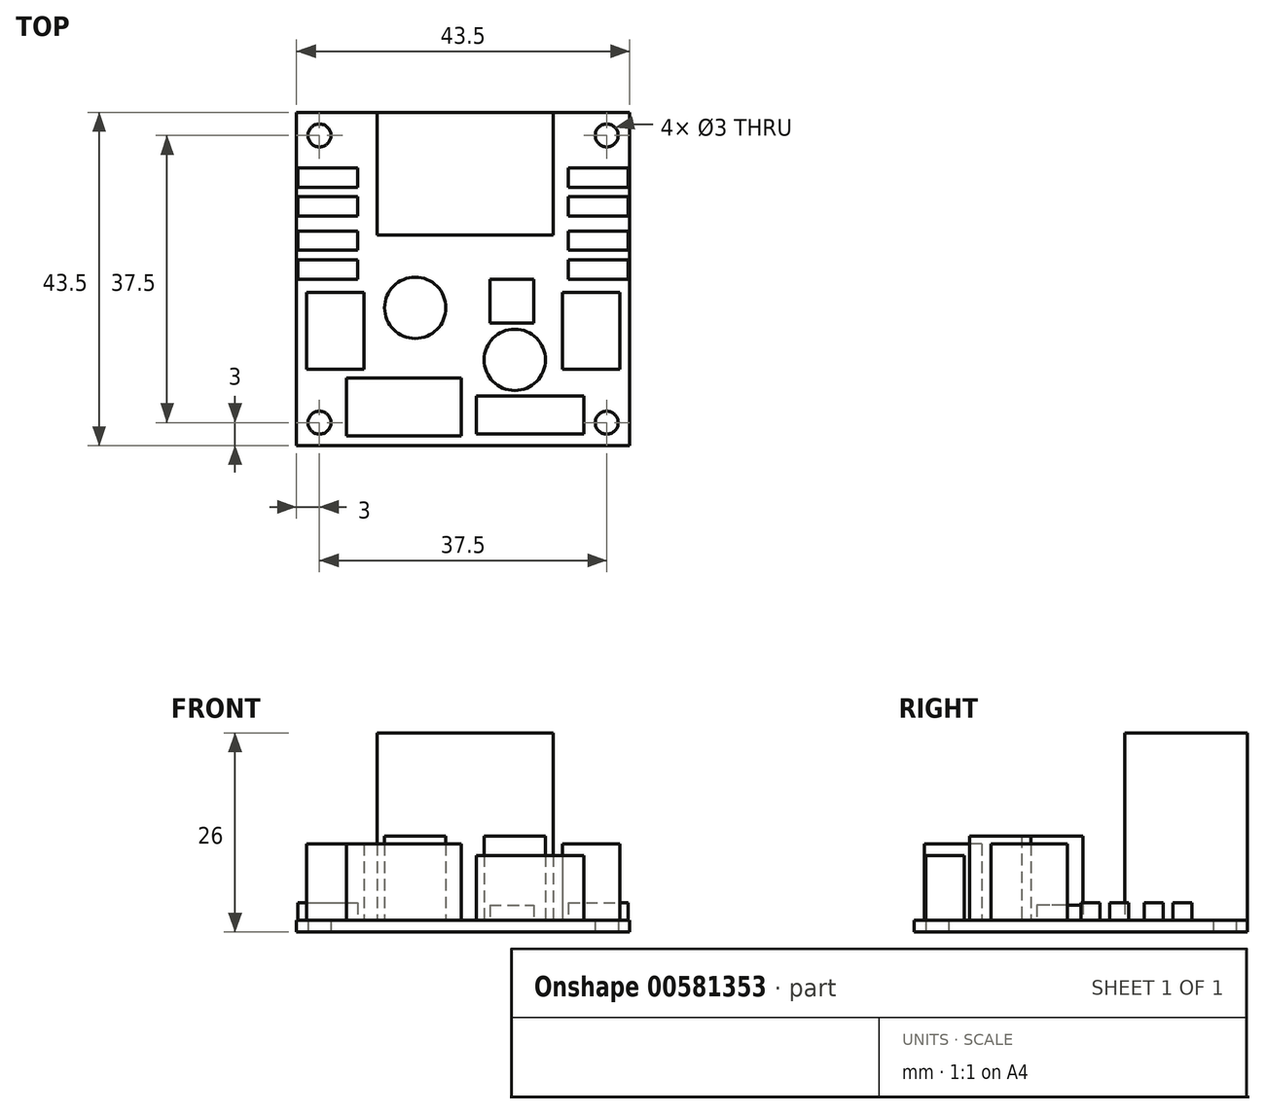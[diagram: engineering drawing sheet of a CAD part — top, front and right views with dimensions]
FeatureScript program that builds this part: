
annotation { "Feature Type Name" : "Feature", "Feature Type Description" : "" }
export const myFeature = defineFeature(function(context is Context, id is Id, definition is map)
    precondition{}
    {
        {
            var Q0;
            Q0=qCreatedBy(makeId("Top.planeOp"),FACE);
            var sketch = newSketch(context, id + "F0", { "sketchPlane" : qUnion([Q0])});
            skLineSegment(sketch, "E0.bottom", {"start": v(-21.75, -21.75) * mm, "end": v(21.75, -21.75) * mm});
            skLineSegment(sketch, "E0.top", {"start": v(-21.75, 21.75) * mm, "end": v(21.75, 21.75) * mm});
            skLineSegment(sketch, "E0.left", {"start": v(-21.75, -21.75) * mm, "end": v(-21.75, 21.75) * mm});
            skLineSegment(sketch, "E0.right", {"start": v(21.75, -21.75) * mm, "end": v(21.75, 21.75) * mm});
            skPoint(sketch, "E0.middle", {"position": v(0, 0) * mm});
            skCircle(sketch, "E1", {"center": v(-18.75, 18.75) * mm, "radius": 1.5 * mm});
            skCircle(sketch, "E2", {"center": v(18.75, 18.75) * mm, "radius": 1.5 * mm});
            skCircle(sketch, "E3", {"center": v(18.75, -18.75) * mm, "radius": 1.5 * mm});
            skCircle(sketch, "E4", {"center": v(-18.75, -18.75) * mm, "radius": 1.5 * mm});
            skSolve(sketch);
        }
        {
            var Q0;
            Q0=makeQuery(id+"F0.imprint","IMPRINT",FACE,{"disambiguationData":[TD([[makeQuery(id+"F0.imprint","IMPRINT",EDGE,{"derivedFrom":sQuery(id+"F0.wireOp",EDGE,"E0.bottom")}),1.0]])]});
            extrude(context, id + "F1", {"entities" : qUnion([Q0]), "depth" : 1.5 * mm, "offsetDistance" : 25 * mm});
        }
        {
            var Q0;
            Q0=makeQuery(id+"F1.opExtrude","CAP_FACE",FACE,{"disambiguationData":[OSD([sQuery(id+"F0.wireOp",EDGE,"E0.bottom"),sQuery(id+"F0.wireOp",EDGE,"E0.top"),sQuery(id+"F0.wireOp",EDGE,"E0.left"),sQuery(id+"F0.wireOp",EDGE,"E0.right"),sQuery(id+"F0.wireOp",EDGE,"E1"),sQuery(id+"F0.wireOp",EDGE,"E2"),sQuery(id+"F0.wireOp",EDGE,"E3"),sQuery(id+"F0.wireOp",EDGE,"E4")])],"isStart":false});
            var sketch = newSketch(context, id + "F2", { "sketchPlane" : qUnion([Q0])});
            skLineSegment(sketch, "E5.bottom", {"start": v(-11.25, 21.75) * mm, "end": v(11.75, 21.75) * mm});
            skLineSegment(sketch, "E5.top", {"start": v(-11.25, 5.75) * mm, "end": v(11.75, 5.75) * mm});
            skLineSegment(sketch, "E5.left", {"start": v(-11.25, 21.75) * mm, "end": v(-11.25, 5.75) * mm});
            skLineSegment(sketch, "E5.right", {"start": v(11.75, 21.75) * mm, "end": v(11.75, 5.75) * mm});
            skSolve(sketch);
        }
        {
            var Q0;
            Q0 = qSketchRegion(id + "F2", true);
            extrude(context, id + "F3", {"entities" : qUnion([Q0]), "operationType" : NewBodyOperationType.ADD, "depth" : 24.5 * mm, "offsetDistance" : 25 * mm});
        }
        {
            var Q0;
            Q0=makeQuery(id+"F1.opExtrude","CAP_FACE",FACE,{"disambiguationData":[OSD([sQuery(id+"F0.wireOp",EDGE,"E0.bottom"),sQuery(id+"F0.wireOp",EDGE,"E0.top"),sQuery(id+"F0.wireOp",EDGE,"E0.left"),sQuery(id+"F0.wireOp",EDGE,"E0.right"),sQuery(id+"F0.wireOp",EDGE,"E1"),sQuery(id+"F0.wireOp",EDGE,"E2"),sQuery(id+"F0.wireOp",EDGE,"E3"),sQuery(id+"F0.wireOp",EDGE,"E4")])],"isStart":false});
            var sketch = newSketch(context, id + "F4", { "sketchPlane" : qUnion([Q0])});
            skLineSegment(sketch, "E6.bottom", {"start": v(-21.75, 14.5) * mm, "end": v(-13.75, 14.5) * mm});
            skLineSegment(sketch, "E6.top", {"start": v(-21.75, 12) * mm, "end": v(-13.75, 12) * mm});
            skLineSegment(sketch, "E6.left", {"start": v(-21.75, 14.5) * mm, "end": v(-21.75, 12) * mm});
            skLineSegment(sketch, "E6.right", {"start": v(-13.75, 14.5) * mm, "end": v(-13.75, 12) * mm});
            skLineSegment(sketch, "E7.bottom", {"start": v(-21.75, 10.75) * mm, "end": v(-13.75, 10.75) * mm});
            skLineSegment(sketch, "E7.top", {"start": v(-21.75, 8.25) * mm, "end": v(-13.75, 8.25) * mm});
            skLineSegment(sketch, "E7.left", {"start": v(-21.75, 10.75) * mm, "end": v(-21.75, 8.25) * mm});
            skLineSegment(sketch, "E7.right", {"start": v(-13.75, 10.75) * mm, "end": v(-13.75, 8.25) * mm});
            skLineSegment(sketch, "E8.bottom", {"start": v(-21.75, 6.25) * mm, "end": v(-13.75, 6.25) * mm});
            skLineSegment(sketch, "E8.top", {"start": v(-21.75, 3.75) * mm, "end": v(-13.75, 3.75) * mm});
            skLineSegment(sketch, "E8.left", {"start": v(-21.75, 6.25) * mm, "end": v(-21.75, 3.75) * mm});
            skLineSegment(sketch, "E8.right", {"start": v(-13.75, 6.25) * mm, "end": v(-13.75, 3.75) * mm});
            skLineSegment(sketch, "E9.bottom", {"start": v(13.75, 14.5) * mm, "end": v(21.75, 14.5) * mm});
            skLineSegment(sketch, "E9.top", {"start": v(13.75, 12) * mm, "end": v(21.75, 12) * mm});
            skLineSegment(sketch, "E9.left", {"start": v(13.75, 14.5) * mm, "end": v(13.75, 12) * mm});
            skLineSegment(sketch, "E9.right", {"start": v(21.75, 14.5) * mm, "end": v(21.75, 12) * mm});
            skLineSegment(sketch, "E10.bottom", {"start": v(13.75, 10.75) * mm, "end": v(21.75, 10.75) * mm});
            skLineSegment(sketch, "E10.top", {"start": v(13.75, 8.25) * mm, "end": v(21.75, 8.25) * mm});
            skLineSegment(sketch, "E10.left", {"start": v(13.75, 10.75) * mm, "end": v(13.75, 8.25) * mm});
            skLineSegment(sketch, "E10.right", {"start": v(21.75, 10.75) * mm, "end": v(21.75, 8.25) * mm});
            skLineSegment(sketch, "E11.bottom", {"start": v(13.75, 6.25) * mm, "end": v(21.75, 6.25) * mm});
            skLineSegment(sketch, "E11.top", {"start": v(13.75, 3.75) * mm, "end": v(21.75, 3.75) * mm});
            skLineSegment(sketch, "E11.left", {"start": v(13.75, 6.25) * mm, "end": v(13.75, 3.75) * mm});
            skLineSegment(sketch, "E11.right", {"start": v(21.75, 6.25) * mm, "end": v(21.75, 3.75) * mm});
            skLineSegment(sketch, "E12.bottom", {"start": v(13.75, 2.5) * mm, "end": v(21.75, 2.5) * mm});
            skLineSegment(sketch, "E12.top", {"start": v(13.75, 0) * mm, "end": v(21.75, 0) * mm});
            skLineSegment(sketch, "E12.left", {"start": v(13.75, 2.5) * mm, "end": v(13.75, 0) * mm});
            skLineSegment(sketch, "E12.right", {"start": v(21.75, 2.5) * mm, "end": v(21.75, 0) * mm});
            skLineSegment(sketch, "E13.bottom", {"start": v(-21.75, 2.5) * mm, "end": v(-13.75, 2.5) * mm});
            skLineSegment(sketch, "E13.top", {"start": v(-21.75, 0) * mm, "end": v(-13.75, 0) * mm});
            skLineSegment(sketch, "E13.left", {"start": v(-21.75, 2.5) * mm, "end": v(-21.75, 0) * mm});
            skLineSegment(sketch, "E13.right", {"start": v(-13.75, 2.5) * mm, "end": v(-13.75, 0) * mm});
            skSolve(sketch);
        }
        {
            var Q0;
            Q0 = qSketchRegion(id + "F4", true);
            extrude(context, id + "F5", {"entities" : qUnion([Q0]), "operationType" : NewBodyOperationType.ADD, "depth" : 2.3 * mm, "offsetDistance" : 25 * mm});
        }
        {
            var Q0;
            Q0=makeQuery(id+"F1.opExtrude","CAP_FACE",FACE,{"disambiguationData":[OSD([sQuery(id+"F0.wireOp",EDGE,"E0.bottom"),sQuery(id+"F0.wireOp",EDGE,"E0.top"),sQuery(id+"F0.wireOp",EDGE,"E0.left"),sQuery(id+"F0.wireOp",EDGE,"E0.right"),sQuery(id+"F0.wireOp",EDGE,"E1"),sQuery(id+"F0.wireOp",EDGE,"E2"),sQuery(id+"F0.wireOp",EDGE,"E3"),sQuery(id+"F0.wireOp",EDGE,"E4")])],"isStart":false});
            var sketch = newSketch(context, id + "F6", { "sketchPlane" : qUnion([Q0])});
            skLineSegment(sketch, "E14.bottom", {"start": v(3.5, 0) * mm, "end": v(9.25, 0) * mm});
            skLineSegment(sketch, "E14.top", {"start": v(3.5, -5.75) * mm, "end": v(9.25, -5.75) * mm});
            skLineSegment(sketch, "E14.left", {"start": v(3.5, 0) * mm, "end": v(3.5, -5.75) * mm});
            skLineSegment(sketch, "E14.right", {"start": v(9.25, 0) * mm, "end": v(9.25, -5.75) * mm});
            skSolve(sketch);
        }
        {
            var Q0;
            Q0 = qSketchRegion(id + "F6", true);
            extrude(context, id + "F7", {"entities" : qUnion([Q0]), "operationType" : NewBodyOperationType.ADD, "depth" : 2 * mm, "offsetDistance" : 25 * mm});
        }
        {
            var Q0;
            Q0=makeQuery(id+"F1.opExtrude","CAP_FACE",FACE,{"disambiguationData":[OSD([sQuery(id+"F0.wireOp",EDGE,"E0.bottom"),sQuery(id+"F0.wireOp",EDGE,"E0.top"),sQuery(id+"F0.wireOp",EDGE,"E0.left"),sQuery(id+"F0.wireOp",EDGE,"E0.right"),sQuery(id+"F0.wireOp",EDGE,"E1"),sQuery(id+"F0.wireOp",EDGE,"E2"),sQuery(id+"F0.wireOp",EDGE,"E3"),sQuery(id+"F0.wireOp",EDGE,"E4")])],"isStart":false});
            var sketch = newSketch(context, id + "F8", { "sketchPlane" : qUnion([Q0])});
            skCircle(sketch, "E15", {"center": v(-6.25, -3.75) * mm, "radius": 4 * mm});
            skCircle(sketch, "E16", {"center": v(6.75, -10.55) * mm, "radius": 4 * mm});
            skSolve(sketch);
        }
        {
            var Q0;
            Q0 = qSketchRegion(id + "F8", true);
            extrude(context, id + "F9", {"entities" : qUnion([Q0]), "operationType" : NewBodyOperationType.ADD, "depth" : 11 * mm, "offsetDistance" : 25 * mm});
        }
        {
            var Q0;
            Q0=makeQuery(id+"F1.opExtrude","CAP_FACE",FACE,{"disambiguationData":[OSD([sQuery(id+"F0.wireOp",EDGE,"E0.bottom"),sQuery(id+"F0.wireOp",EDGE,"E0.top"),sQuery(id+"F0.wireOp",EDGE,"E0.left"),sQuery(id+"F0.wireOp",EDGE,"E0.right"),sQuery(id+"F0.wireOp",EDGE,"E1"),sQuery(id+"F0.wireOp",EDGE,"E2"),sQuery(id+"F0.wireOp",EDGE,"E3"),sQuery(id+"F0.wireOp",EDGE,"E4")])],"isStart":false});
            var sketch = newSketch(context, id + "F10", { "sketchPlane" : qUnion([Q0])});
            skLineSegment(sketch, "E17.bottom", {"start": v(12.95, -1.75) * mm, "end": v(20.45, -1.75) * mm});
            skLineSegment(sketch, "E17.top", {"start": v(12.95, -11.75) * mm, "end": v(20.45, -11.75) * mm});
            skLineSegment(sketch, "E17.left", {"start": v(12.95, -1.75) * mm, "end": v(12.95, -11.75) * mm});
            skLineSegment(sketch, "E17.right", {"start": v(20.45, -1.75) * mm, "end": v(20.45, -11.75) * mm});
            skLineSegment(sketch, "E18.bottom", {"start": v(-20.45, -1.75) * mm, "end": v(-12.95, -1.75) * mm});
            skLineSegment(sketch, "E18.top", {"start": v(-20.45, -11.75) * mm, "end": v(-12.95, -11.75) * mm});
            skLineSegment(sketch, "E18.left", {"start": v(-20.45, -1.75) * mm, "end": v(-20.45, -11.75) * mm});
            skLineSegment(sketch, "E18.right", {"start": v(-12.95, -1.75) * mm, "end": v(-12.95, -11.75) * mm});
            skLineSegment(sketch, "E19.bottom", {"start": v(-15.25, -12.95) * mm, "end": v(-0.25, -12.95) * mm});
            skLineSegment(sketch, "E19.top", {"start": v(-15.25, -20.45) * mm, "end": v(-0.25, -20.45) * mm});
            skLineSegment(sketch, "E19.left", {"start": v(-15.25, -12.95) * mm, "end": v(-15.25, -20.45) * mm});
            skLineSegment(sketch, "E19.right", {"start": v(-0.25, -12.95) * mm, "end": v(-0.25, -20.45) * mm});
            skSolve(sketch);
        }
        {
            var Q0;
            Q0 = qSketchRegion(id + "F10", true);
            extrude(context, id + "F11", {"entities" : qUnion([Q0]), "operationType" : NewBodyOperationType.ADD, "depth" : 10 * mm, "offsetDistance" : 25 * mm});
        }
        {
            var Q0;
            Q0=makeQuery(id+"F1.opExtrude","CAP_FACE",FACE,{"disambiguationData":[OSD([sQuery(id+"F0.wireOp",EDGE,"E0.bottom"),sQuery(id+"F0.wireOp",EDGE,"E0.top"),sQuery(id+"F0.wireOp",EDGE,"E0.left"),sQuery(id+"F0.wireOp",EDGE,"E0.right"),sQuery(id+"F0.wireOp",EDGE,"E1"),sQuery(id+"F0.wireOp",EDGE,"E2"),sQuery(id+"F0.wireOp",EDGE,"E3"),sQuery(id+"F0.wireOp",EDGE,"E4")])],"isStart":false});
            var sketch = newSketch(context, id + "F12", { "sketchPlane" : qUnion([Q0])});
            skLineSegment(sketch, "E20.bottom", {"start": v(1.75, -15.25) * mm, "end": v(15.75, -15.25) * mm});
            skLineSegment(sketch, "E20.top", {"start": v(1.75, -20.25) * mm, "end": v(15.75, -20.25) * mm});
            skLineSegment(sketch, "E20.left", {"start": v(1.75, -15.25) * mm, "end": v(1.75, -20.25) * mm});
            skLineSegment(sketch, "E20.right", {"start": v(15.75, -15.25) * mm, "end": v(15.75, -20.25) * mm});
            skSolve(sketch);
        }
        {
            var Q0;
            Q0=makeQuery(id+"F12.imprint","IMPRINT",FACE,{"disambiguationData":[TD([[makeQuery(id+"F12.imprint","IMPRINT",EDGE,{"derivedFrom":sQuery(id+"F12.wireOp",EDGE,"E20.bottom")}),-1.0]])]});
            extrude(context, id + "F13", {"entities" : qUnion([Q0]), "operationType" : NewBodyOperationType.ADD, "depth" : 8.5 * mm, "offsetDistance" : 25 * mm});
        }
        {
            var Q0;
            Q0=makeQuery(id+"F5.boolean.opBoolean","MERGE",FACE,{"derivedFrom":[makeQuery(id+"F1.opExtrude","SWEPT_FACE",FACE,{"disambiguationData":[OSD([sQuery(id+"F0.wireOp",EDGE,"E0.right")])]}),makeQuery(id+"F5.opExtrude","SWEPT_FACE",FACE,{"disambiguationData":[OSD([sQuery(id+"F4.wireOp",EDGE,"E9.right")])]}),makeQuery(id+"F5.opExtrude","SWEPT_FACE",FACE,{"disambiguationData":[OSD([sQuery(id+"F4.wireOp",EDGE,"E10.right")])]}),makeQuery(id+"F5.opExtrude","SWEPT_FACE",FACE,{"disambiguationData":[OSD([sQuery(id+"F4.wireOp",EDGE,"E11.right")])]}),makeQuery(id+"F5.opExtrude","SWEPT_FACE",FACE,{"disambiguationData":[OSD([sQuery(id+"F4.wireOp",EDGE,"E12.right")])]})]});
            var sketch = newSketch(context, id + "F14", { "sketchPlane" : qUnion([Q0])});
            skLineSegment(sketch, "E21", {"start": v(0, 1.5) * mm, "end": v(14.5, 1.5) * mm});
            skSolve(sketch);
        }
        {
            var Q0;
            {var subQ1=sQuery(id+"F4.wireOp",EDGE,"E12.right");Q0=makeQuery(id+"F14.imprint","IMPRINT",FACE,{"disambiguationData":[TD([[makeQuery(id+"F14.imprint","IMPRINT",EDGE,{"derivedFrom":makeQuery(id+"F5.opExtrude","CAP_EDGE",EDGE,{"disambiguationData":[OSD([subQ1])],"isStart":false})}),-1.0]])]});}
            var Q1;
            {var subQ1=sQuery(id+"F4.wireOp",EDGE,"E11.right");Q1=makeQuery(id+"F14.imprint","IMPRINT",FACE,{"disambiguationData":[TD([[makeQuery(id+"F14.imprint","IMPRINT",EDGE,{"derivedFrom":makeQuery(id+"F5.opExtrude","CAP_EDGE",EDGE,{"disambiguationData":[OSD([subQ1])],"isStart":false})}),-1.0]])]});}
            var Q2;
            {var subQ1=sQuery(id+"F4.wireOp",EDGE,"E10.right");Q2=makeQuery(id+"F14.imprint","IMPRINT",FACE,{"disambiguationData":[TD([[makeQuery(id+"F14.imprint","IMPRINT",EDGE,{"derivedFrom":makeQuery(id+"F5.opExtrude","CAP_EDGE",EDGE,{"disambiguationData":[OSD([subQ1])],"isStart":false})}),-1.0]])]});}
            var Q3;
            {var subQ4=sQuery(id+"F4.wireOp",EDGE,"E9.right");Q3=makeQuery(id+"F14.imprint","IMPRINT",FACE,{"disambiguationData":[TD([[makeQuery(id+"F14.imprint","IMPRINT",EDGE,{"derivedFrom":makeQuery(id+"F5.opExtrude","CAP_EDGE",EDGE,{"disambiguationData":[OSD([subQ4])],"isStart":false})}),-1.0]])]});}
            extrude(context, id + "F15", {"entities" : qUnion([Q0, Q1, Q2, Q3]), "operationType" : NewBodyOperationType.REMOVE, "oppositeDirection" : true, "depth" : 0.2 * mm, "offsetDistance" : 25 * mm});
        }
        {
            var Q0;
            Q0=makeQuery(id+"F5.boolean.opBoolean","MERGE",FACE,{"derivedFrom":[makeQuery(id+"F1.opExtrude","SWEPT_FACE",FACE,{"disambiguationData":[OSD([sQuery(id+"F0.wireOp",EDGE,"E0.left")])]}),makeQuery(id+"F5.opExtrude","SWEPT_FACE",FACE,{"disambiguationData":[OSD([sQuery(id+"F4.wireOp",EDGE,"E6.left")])]}),makeQuery(id+"F5.opExtrude","SWEPT_FACE",FACE,{"disambiguationData":[OSD([sQuery(id+"F4.wireOp",EDGE,"E7.left")])]}),makeQuery(id+"F5.opExtrude","SWEPT_FACE",FACE,{"disambiguationData":[OSD([sQuery(id+"F4.wireOp",EDGE,"E8.left")])]}),makeQuery(id+"F5.opExtrude","SWEPT_FACE",FACE,{"disambiguationData":[OSD([sQuery(id+"F4.wireOp",EDGE,"E13.left")])]})]});
            var sketch = newSketch(context, id + "F16", { "sketchPlane" : qUnion([Q0])});
            skLineSegment(sketch, "E22", {"start": v(-14.5, 1.5) * mm, "end": v(0, 1.5) * mm});
            skSolve(sketch);
        }
        {
            var Q0;
            {var subQ4=sQuery(id+"F4.wireOp",EDGE,"E6.left");Q0=makeQuery(id+"F16.imprint","IMPRINT",FACE,{"disambiguationData":[TD([[makeQuery(id+"F16.imprint","IMPRINT",EDGE,{"derivedFrom":makeQuery(id+"F5.opExtrude","CAP_EDGE",EDGE,{"disambiguationData":[OSD([subQ4])],"isStart":false})}),1.0]])]});}
            var Q1;
            {var subQ1=sQuery(id+"F4.wireOp",EDGE,"E7.left");Q1=makeQuery(id+"F16.imprint","IMPRINT",FACE,{"disambiguationData":[TD([[makeQuery(id+"F16.imprint","IMPRINT",EDGE,{"derivedFrom":makeQuery(id+"F5.opExtrude","CAP_EDGE",EDGE,{"disambiguationData":[OSD([subQ1])],"isStart":false})}),1.0]])]});}
            var Q2;
            {var subQ1=sQuery(id+"F4.wireOp",EDGE,"E8.left");Q2=makeQuery(id+"F16.imprint","IMPRINT",FACE,{"disambiguationData":[TD([[makeQuery(id+"F16.imprint","IMPRINT",EDGE,{"derivedFrom":makeQuery(id+"F5.opExtrude","CAP_EDGE",EDGE,{"disambiguationData":[OSD([subQ1])],"isStart":false})}),1.0]])]});}
            var Q3;
            {var subQ1=sQuery(id+"F4.wireOp",EDGE,"E13.left");Q3=makeQuery(id+"F16.imprint","IMPRINT",FACE,{"disambiguationData":[TD([[makeQuery(id+"F16.imprint","IMPRINT",EDGE,{"derivedFrom":makeQuery(id+"F5.opExtrude","CAP_EDGE",EDGE,{"disambiguationData":[OSD([subQ1])],"isStart":false})}),1.0]])]});}
            extrude(context, id + "F17", {"entities" : qUnion([Q0, Q1, Q2, Q3]), "operationType" : NewBodyOperationType.REMOVE, "oppositeDirection" : true, "depth" : 0.2 * mm, "offsetDistance" : 25 * mm});
        }
    });
